# Revit family: AFX-Addison-Linear_Ceiling
name_source: partatom
category: Lighting Fixtures
units: mm (PartAtom-declared; Revit-internal decimal feet)

## family parameters
Cut with Voids When Loaded = No
Host = Face
Light Source = Yes
Part Type = Normal
Room Calculation Point = No
Round Connector Dimension = Use Diameter
Shared = No

## types (1)
- ADDL1248LAJD1WH
    Apparent Load = 0 VA
    Assembly Code = D5020200
    Color Filter = 16777215
    Colour Rendering Index = 90
    Default Elevation = 48"
    Description = Modern LED Linear Ceiling Mount Frameless Design White Polycarbonate Diffuser - 12"W x 1 1/8"D x 48"L
    Diffuser Finish = AFX - White Acrylic
    Dimming Lamp Color Temperature Shift = <None>
    Emit Shape Visible in Rendering = No
    Emit from Rectangle Length = 48"
    Emit from Rectangle Width = 10"
    Frame Finish = AFX - White Steel
    Height = 1 1/8"
    Keynote = 12500
    Length = 48"
    Manufacturer = AFX Inc
    Model = ADDL1248LAJD1WH
    Photometric Web File = ADDL1248LAJD1WH_3000K_HIGH_IES.ies
    Power Factor = 1
    Product Documentation Link = https://www.afxinc.com
    Revit File Built By = https://servex-us.com
    Tilt Angle = 90.00°
    Type Comments = Addison
    URL = https://www.afxinc.com
    Voltage = 120 V
    Wattage Comments = 40
    Width = 12"

## geometry (parser evidence)
native form markers: Sweep x2
no freeform markers — native parametric forms only
